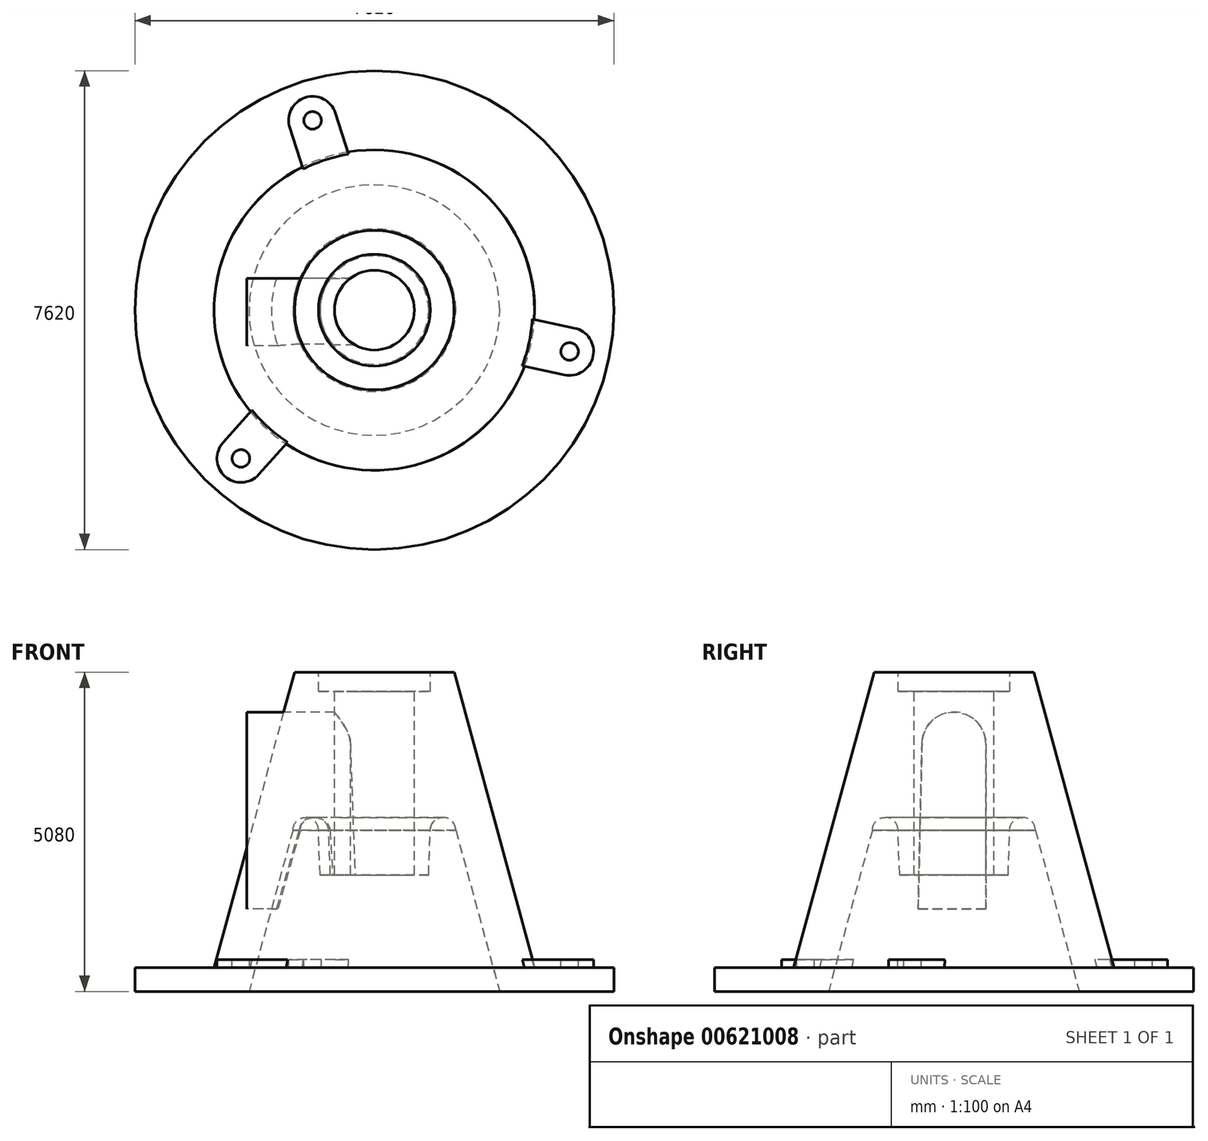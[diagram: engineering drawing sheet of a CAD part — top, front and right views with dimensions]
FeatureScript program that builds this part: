
annotation { "Feature Type Name" : "Feature", "Feature Type Description" : "" }
export const myFeature = defineFeature(function(context is Context, id is Id, definition is map)
    precondition{}
    {
        {
            var Q0;
            Q0=qCreatedBy(makeId("Front.planeOp"),FACE);
            var sketch = newSketch(context, id + "F0", { "sketchPlane" : qUnion([Q0])});
            skLineSegment(sketch, "E0", {"start": v(0, 0) * mm, "end": v(1270, 0) * mm});
            skLineSegment(sketch, "E1", {"start": v(0, 0) * mm, "end": v(889, 0) * mm});
            skLineSegment(sketch, "E2", {"start": v(889, 0) * mm, "end": v(889, -304.8) * mm});
            skLineSegment(sketch, "E3", {"start": v(0, 0) * mm, "end": v(0, -9485.62) * mm, "construction": true});
            skLineSegment(sketch, "E4", {"start": v(889, -304.8) * mm, "end": v(0, -304.8) * mm});
            skLineSegment(sketch, "E5", {"start": v(0, -304.8) * mm, "end": v(635, -304.8) * mm});
            skLineSegment(sketch, "E6", {"start": v(635, -304.8) * mm, "end": v(635, -3225.8) * mm});
            skLineSegment(sketch, "E7", {"start": v(635, -3225.8) * mm, "end": v(0, -3225.8) * mm});
            skLineSegment(sketch, "E8", {"start": v(0, -3225.8) * mm, "end": v(863.6, -3225.8) * mm});
            skLineSegment(sketch, "E9", {"start": v(0, -5080) * mm, "end": v(0, -2514.6) * mm});
            skLineSegment(sketch, "E10", {"start": v(0, -2514.6) * mm, "end": v(889, -2514.6) * mm, "construction": true});
            skArc(sketch, "E11", {"start": v(1295.4, -2514.6) * mm, "mid": v(1092.2, -2311.4) * mm, "end": v(889, -2514.6) * mm});
            skLineSegment(sketch, "E12", {"start": v(889, -2514.6) * mm, "end": v(863.6, -3225.8) * mm});
            skLineSegment(sketch, "E13", {"start": v(1295.4, -2514.6) * mm, "end": v(1993.9, -5080) * mm});
            skLineSegment(sketch, "E14", {"start": v(1993.9, -5080) * mm, "end": v(3810, -5080) * mm});
            skLineSegment(sketch, "E15", {"start": v(3810, -5080) * mm, "end": v(3810, -4699) * mm});
            skLineSegment(sketch, "E16", {"start": v(3810, -4699) * mm, "end": v(2549.43, -4699) * mm});
            skLineSegment(sketch, "E17", {"start": v(1270, 0) * mm, "end": v(2549.43, -4699) * mm});
            skSolve(sketch);
        }
        {
            var Q0;
            Q0=makeQuery(id+"F0.imprint","IMPRINT",FACE,{"disambiguationData":[TD([[makeQuery(id+"F0.imprint","IMPRINT",EDGE,{"derivedFrom":sQuery(id+"F0.wireOp",EDGE,"E0")}),-1.0]])]});
            var Q1;
            Q1=sQuery(id+"F0.wireOp",EDGE,"E3");
            revolve(context, id + "F1", {"entities" : qUnion([Q0]), "axis" : qUnion([Q1]), "revolveType" : RevolveType.FULL});
        }
        {
            var Q0;
            Q0=qCreatedBy(makeId("Top.planeOp"),FACE);
            cPlane(context, id + "F2", {"entities" : qUnion([Q0]), "cplaneType" : CPlaneType.OFFSET, "offset" : 4572 * mm, "oppositeDirection" : true, "width" : 152.4 * mm, "height" : 152.4 * mm});
        }
        {
            var Q0;
            Q0=qCreatedBy(id+"F2.planeOp",FACE);
            var sketch = newSketch(context, id + "F3", { "sketchPlane" : qUnion([Q0])});
            skCircle(sketch, "E18", {"center": v(0, 0) * mm, "radius": 3175 * mm, "construction": true});
            skLineSegment(sketch, "E19", {"start": v(0, 0) * mm, "end": v(-2123.26, -2360.6) * mm, "construction": true});
            skLineSegment(sketch, "E20", {"start": v(0, 0) * mm, "end": v(-982.7, 3019.1) * mm, "construction": true});
            skArc(sketch, "E21", {"start": v(-620.42, 3137.02) * mm, "mid": v(-1100.63, 3381.38) * mm, "end": v(-1345, 2901.17) * mm});
            skLineSegment(sketch, "E22", {"start": v(-620.42, 3137.02) * mm, "end": v(-362.51, 2344.68) * mm});
            skLineSegment(sketch, "E23", {"start": v(-1345, 2901.17) * mm, "end": v(-1060.32, 2026.58) * mm});
            skLineSegment(sketch, "E24", {"start": v(-1060.32, 2026.58) * mm, "end": v(-362.51, 2344.68) * mm});
            skCircle(sketch, "E25", {"center": v(-982.7, 3019.1) * mm, "radius": 139.7 * mm});
            skSolve(sketch);
        }
        {
            var Q0;
            Q0=makeQuery(id+"F3.imprint","IMPRINT",FACE,{"disambiguationData":[TD([[makeQuery(id+"F3.imprint","IMPRINT",EDGE,{"derivedFrom":sQuery(id+"F3.wireOp",EDGE,"E21")}),1.0]])]});
            extrude(context, id + "F4", {"entities" : qUnion([Q0]), "operationType" : NewBodyOperationType.ADD, "oppositeDirection" : true, "depth" : 127 * mm, "offsetDistance" : 25.4 * mm});
        }
        {
            var Q0;
            Q0=makeQuery(id+"F1.opRevolve","SWEPT_BODY",BODY,{"disambiguationData":[OSD([sQuery(id+"F0.wireOp",EDGE,"E0"),sQuery(id+"F0.wireOp",EDGE,"E2"),sQuery(id+"F0.wireOp",EDGE,"E4"),sQuery(id+"F0.wireOp",EDGE,"E6"),sQuery(id+"F0.wireOp",EDGE,"E8"),sQuery(id+"F0.wireOp",EDGE,"E11"),sQuery(id+"F0.wireOp",EDGE,"E12"),sQuery(id+"F0.wireOp",EDGE,"E13"),sQuery(id+"F0.wireOp",EDGE,"E14"),sQuery(id+"F0.wireOp",EDGE,"E15"),sQuery(id+"F0.wireOp",EDGE,"E16"),sQuery(id+"F0.wireOp",EDGE,"E17")])]});
            var Q1;
            Q1=sQuery(id+"F0.wireOp",EDGE,"E3");
            circularPattern(context, id + "F5", {"entities" : qUnion([Q0]), "axis" : qUnion([Q1]), "angle" : 360 * degree, "instanceCount" : 3, "equalSpace" : true});
        }
        {
            var Q0;
            Q0=qCreatedBy(makeId("Right.planeOp"),FACE);
            cPlane(context, id + "F6", {"entities" : qUnion([Q0]), "cplaneType" : CPlaneType.OFFSET, "offset" : 2032 * mm, "oppositeDirection" : true, "width" : 152.4 * mm, "height" : 152.4 * mm});
        }
        {
            var Q0;
            Q0=qCreatedBy(id+"F6.planeOp",FACE);
            var sketch = newSketch(context, id + "F7", { "sketchPlane" : qUnion([Q0])});
            skLineSegment(sketch, "E26.0", {"start": v(-3810, -5080) * mm, "end": v(3810, -5080) * mm, "construction": true});
            skPoint(sketch, "E27", {"position": v(0, -5080) * mm});
            skLineSegment(sketch, "E28", {"start": v(0, -5080) * mm, "end": v(0, -1143) * mm, "construction": true});
            skArc(sketch, "E29", {"start": v(508, -1143) * mm, "mid": v(5.8, -635.03) * mm, "end": v(-507.87, -1131.4) * mm});
            skLineSegment(sketch, "E30", {"start": v(508, -1143) * mm, "end": v(508, -3768.66) * mm});
            skLineSegment(sketch, "E31", {"start": v(508, -3768.66) * mm, "end": v(-568.15, -3768.66) * mm});
            skLineSegment(sketch, "E32", {"start": v(-568.15, -3768.66) * mm, "end": v(-507.87, -1131.4) * mm});
            skSolve(sketch);
        }
        {
            var Q0;
            Q0=makeQuery(id+"F7.imprint","IMPRINT",FACE,{"disambiguationData":[TD([[makeQuery(id+"F7.imprint","IMPRINT",EDGE,{"derivedFrom":sQuery(id+"F7.wireOp",EDGE,"E29")}),1.0]])]});
            var Q1;
            Q1=makeQuery(id+"F5.opPattern","COPY",FACE,{"derivedFrom":makeQuery(id+"F1.opRevolve","SWEPT_FACE",FACE,{"disambiguationData":[OSD([sQuery(id+"F0.wireOp",EDGE,"E17")])]}),"instanceName":"2"});
            var Q2;
            Q2=makeQuery(id+"F1.opRevolve","SWEPT_BODY",BODY,{"disambiguationData":[OSD([sQuery(id+"F0.wireOp",EDGE,"E0"),sQuery(id+"F0.wireOp",EDGE,"E2"),sQuery(id+"F0.wireOp",EDGE,"E4"),sQuery(id+"F0.wireOp",EDGE,"E6"),sQuery(id+"F0.wireOp",EDGE,"E8"),sQuery(id+"F0.wireOp",EDGE,"E11"),sQuery(id+"F0.wireOp",EDGE,"E12"),sQuery(id+"F0.wireOp",EDGE,"E13"),sQuery(id+"F0.wireOp",EDGE,"E14"),sQuery(id+"F0.wireOp",EDGE,"E15"),sQuery(id+"F0.wireOp",EDGE,"E16"),sQuery(id+"F0.wireOp",EDGE,"E17")])]});
            extrude(context, id + "F8", {"entities" : qUnion([Q0]), "endBound" : BoundingType.UP_TO_BODY, "depth" : 1270 * mm, "endBoundEntityFace" : qUnion([Q1]), "endBoundEntityBody" : qUnion([Q2]), "offsetDistance" : 25.4 * mm});
        }
    });
